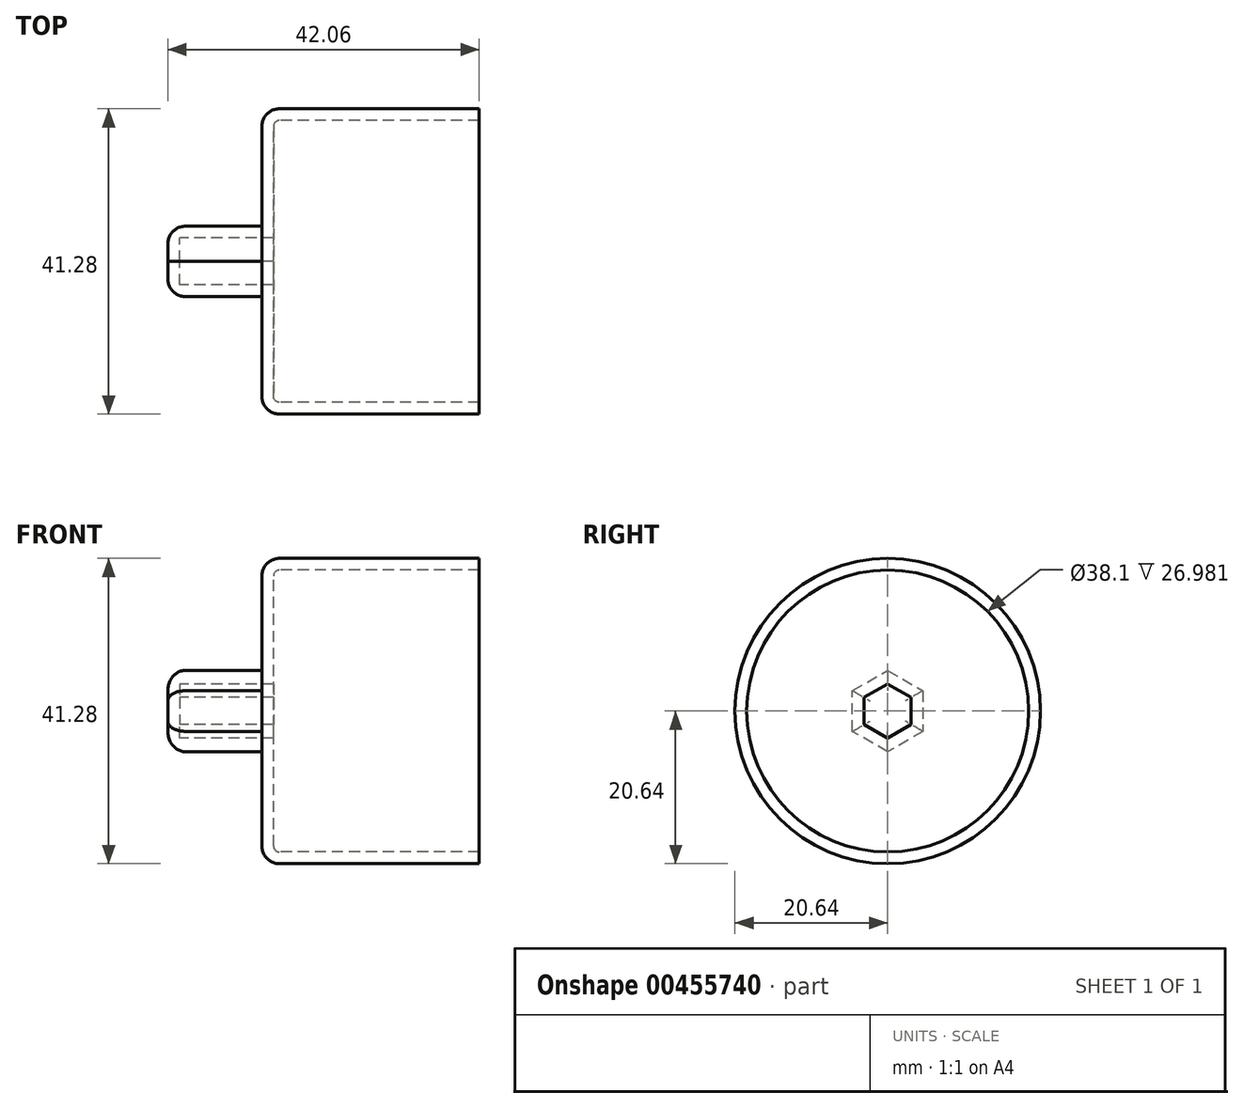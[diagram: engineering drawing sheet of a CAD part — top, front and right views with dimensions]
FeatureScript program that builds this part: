
annotation { "Feature Type Name" : "Feature", "Feature Type Description" : "" }
export const myFeature = defineFeature(function(context is Context, id is Id, definition is map)
    precondition{}
    {
        {
            var Q0;
            Q0=qCreatedBy(makeId("Right.planeOp"),FACE);
            var sketch = newSketch(context, id + "F0", { "sketchPlane" : qUnion([Q0])});
            skCircle(sketch, "E0.cCircle", {"center": v(0, 0) * mm, "radius": 4.76 * mm, "construction": true});
            skLineSegment(sketch, "E0.0", {"start": v(4.76, 2.75) * mm, "end": v(4.76, -2.75) * mm});
            skLineSegment(sketch, "E0.1", {"start": v(4.76, -2.75) * mm, "end": v(0, -5.5) * mm});
            skLineSegment(sketch, "E0.2", {"start": v(0, -5.5) * mm, "end": v(-4.76, -2.75) * mm});
            skLineSegment(sketch, "E0.3", {"start": v(-4.76, -2.75) * mm, "end": v(-4.76, 2.75) * mm});
            skLineSegment(sketch, "E0.4", {"start": v(-4.76, 2.75) * mm, "end": v(0, 5.5) * mm});
            skLineSegment(sketch, "E0.5", {"start": v(0, 5.5) * mm, "end": v(4.76, 2.75) * mm});
            skPoint(sketch, "E0.0.midPoint", {"position": v(4.76, 0) * mm});
            skSolve(sketch);
        }
        {
            var Q0;
            Q0 = qSketchRegion(id + "F0", true);
            extrude(context, id + "F1", {"entities" : qUnion([Q0]), "depth" : 12.7 * mm});
        }
        {
            var Q0;
            Q0=makeQuery(id+"F1.opExtrude","CAP_FACE",FACE,{"disambiguationData":[OSD([sQuery(id+"F0.wireOp",EDGE,"E0.0"),sQuery(id+"F0.wireOp",EDGE,"E0.1"),sQuery(id+"F0.wireOp",EDGE,"E0.2"),sQuery(id+"F0.wireOp",EDGE,"E0.3"),sQuery(id+"F0.wireOp",EDGE,"E0.4"),sQuery(id+"F0.wireOp",EDGE,"E0.5")])],"isStart":false});
            var sketch = newSketch(context, id + "F2", { "sketchPlane" : qUnion([Q0])});
            skCircle(sketch, "E1", {"center": v(0, 0) * mm, "radius": 20.64 * mm});
            skSolve(sketch);
        }
        {
            var Q0;
            Q0 = qSketchRegion(id + "F2", true);
            extrude(context, id + "F3", {"entities" : qUnion([Q0]), "operationType" : NewBodyOperationType.ADD, "depth" : 29.36 * mm, "offsetDistance" : 25.4 * mm});
        }
        {
            var Q0;
            Q0=makeQuery(id+"F3.opExtrude","CAP_FACE",FACE,{"disambiguationData":[OSD([sQuery(id+"F2.wireOp",EDGE,"E1")])],"isStart":false});
            shell(context, id + "F4", {"entities" : qUnion([Q0]), "thickness" : 1.59 * mm});
        }
        {
            var Q0;
            {var subQ0=sQuery(id+"F2.wireOp",EDGE,"E1");Q0=makeQuery(id+"F4.opShell","OFFSET_EDGE",EDGE,{"disambiguationData":[OSD([subQ0]),TDD([makeQuery(id+"F3.opExtrude","CAP_EDGE",EDGE,{"disambiguationData":[OSD([subQ0])],"isStart":true})])]});}
            fillet(context, id + "F5", {"entities" : qUnion([Q0]), "radius" : 0.8 * mm, "tangentPropagation" : true, "allowEdgeOverflow" : false});
        }
        {
            var Q0;
            Q0=makeQuery(id+"F3.opExtrude","CAP_EDGE",EDGE,{"disambiguationData":[OSD([sQuery(id+"F2.wireOp",EDGE,"E1")])],"isStart":true});
            fillet(context, id + "F6", {"entities" : qUnion([Q0]), "radius" : 2.38 * mm, "tangentPropagation" : true, "allowEdgeOverflow" : false});
        }
        {
            var Q0;
            Q0=makeQuery(id+"F1.opExtrude","CAP_EDGE",EDGE,{"disambiguationData":[OSD([sQuery(id+"F0.wireOp",EDGE,"E0.5")])],"isStart":true});
            var Q1;
            Q1=makeQuery(id+"F1.opExtrude","CAP_EDGE",EDGE,{"disambiguationData":[OSD([sQuery(id+"F0.wireOp",EDGE,"E0.4")])],"isStart":true});
            var Q2;
            Q2=makeQuery(id+"F1.opExtrude","CAP_EDGE",EDGE,{"disambiguationData":[OSD([sQuery(id+"F0.wireOp",EDGE,"E0.3")])],"isStart":true});
            var Q3;
            Q3=makeQuery(id+"F1.opExtrude","CAP_EDGE",EDGE,{"disambiguationData":[OSD([sQuery(id+"F0.wireOp",EDGE,"E0.2")])],"isStart":true});
            var Q4;
            Q4=makeQuery(id+"F1.opExtrude","CAP_EDGE",EDGE,{"disambiguationData":[OSD([sQuery(id+"F0.wireOp",EDGE,"E0.1")])],"isStart":true});
            var Q5;
            Q5=makeQuery(id+"F1.opExtrude","CAP_EDGE",EDGE,{"disambiguationData":[OSD([sQuery(id+"F0.wireOp",EDGE,"E0.0")])],"isStart":true});
            fillet(context, id + "F7", {"entities" : qUnion([Q0, Q1, Q2, Q3, Q4, Q5]), "radius" : 2.38 * mm, "tangentPropagation" : true, "allowEdgeOverflow" : false});
        }
    });
